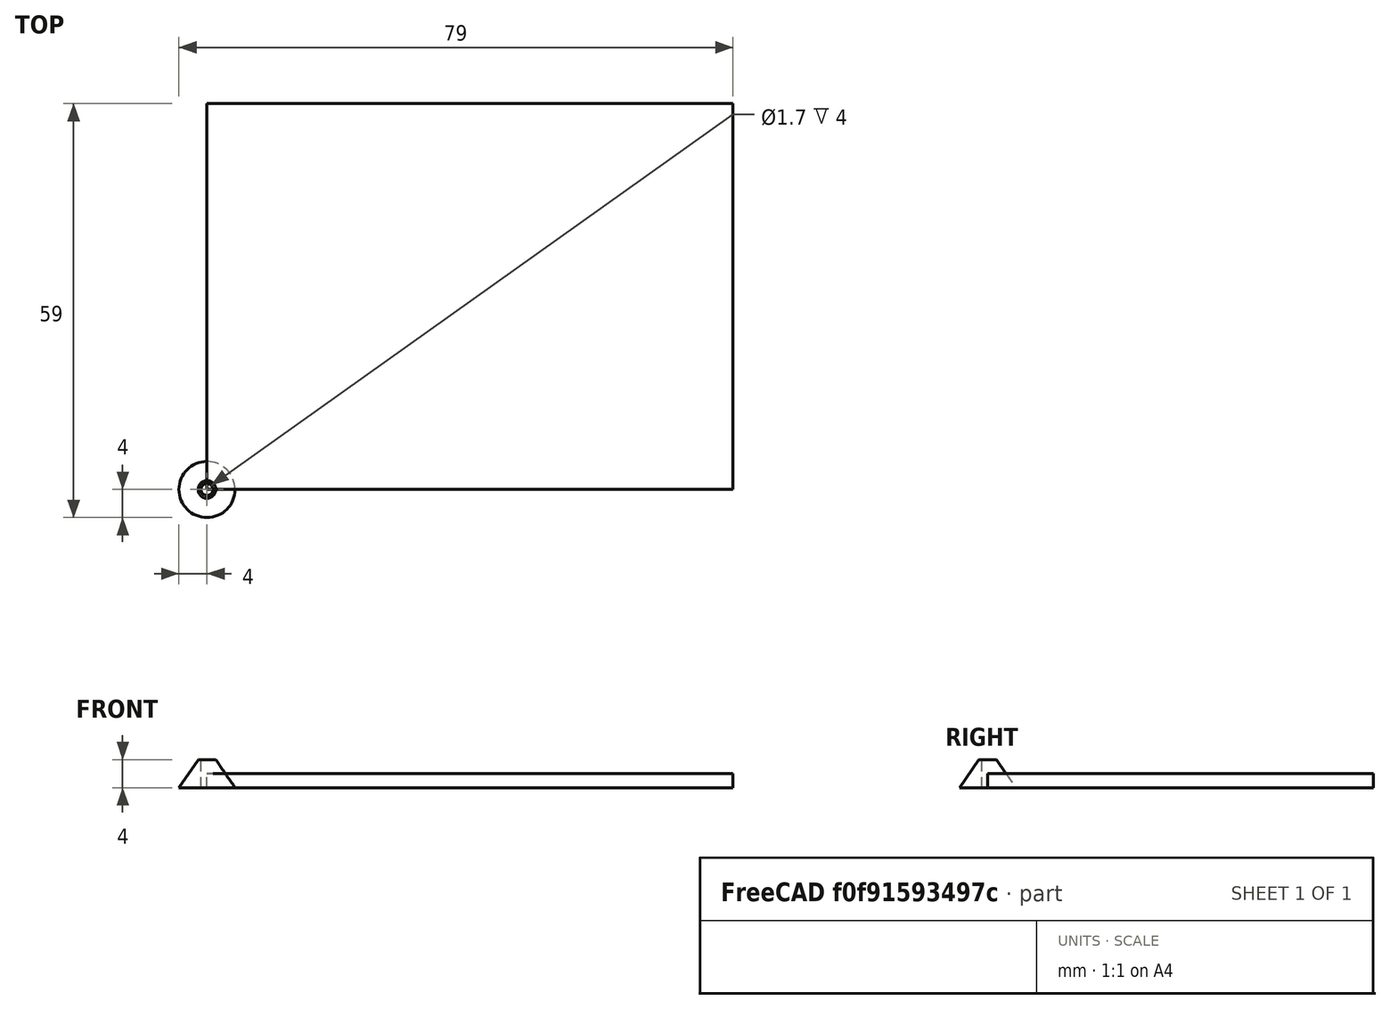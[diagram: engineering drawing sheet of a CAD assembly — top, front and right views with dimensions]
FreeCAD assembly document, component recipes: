
FREECAD ASSEMBLY — COMPONENT RECIPES ("perfboard-standoffs")

This assembly document has 5 components, labeled P0..P4 below (a component is one placed body or linked part). 5 of them carry a construction recipe — the FreeCAD feature program that regenerates the part from scratch, quoted from this document or its linked companion documents; the rest are supplied as boundary geometry only. No exploded tour is included for this assembly.
COMPONENT P0 — recipe-attached ("Body", modeled in this document).
Construction recipe (the document's own serialized feature program — sketch geometry with constraints, then the solid features built on it; lengths are millimeters unless a unit is written):

FEATURE [Sketcher::SketchObject] Sketch003
  ArcFitTolerance = 1e-06
  AttachmentSupport = -> [XY_Plane005]
  FullyConstrained = true
  MakeInternals = false
  MapMode = 5
  sketch-geometry (4):
    g0: LineSegment StartX=0 StartY=0 StartZ=0 EndX=75 EndY=0 EndZ=0
    g1: LineSegment StartX=75 StartY=0 StartZ=0 EndX=75 EndY=55 EndZ=0
    g2: LineSegment StartX=75 StartY=55 StartZ=0 EndX=0 EndY=55 EndZ=0
    g3: LineSegment StartX=0 StartY=55 StartZ=0 EndX=0 EndY=0 EndZ=0
  constraints (11):
    c: Coincident(g0,g1)
    c: Coincident(g1,g2)
    c: Coincident(g2,g3)
    c: Coincident(g3,g0)
    c: Horizontal(g0)
    c: Horizontal(g2)
    c: Vertical(g1)
    c: Vertical(g3)
    c: Distance(g1,g3) = 75
    c: Distance(g0,g2) = 55
    c: Coincident(g0,g-1)
FEATURE [PartDesign::Pad] Pad
  Direction = (0,0,1)
  Length = 2
  Length2 = 10
  Profile = -> Sketch003
  ReferenceAxis = -> Sketch003 [N_Axis]
  Refine = true
  Suppressed = false
  Type = 0
FEATURE [PartDesign::Body] Body001  label="Body"
  AllowCompound = false
  Group = -> [Sketch003,Pad]
  Origin = -> Origin005
  Tip = -> Pad
COMPONENT P1 — recipe-attached ("standoff001", modeled in this document).
Construction recipe (the document's own serialized feature program — sketch geometry with constraints, then the solid features built on it; lengths are millimeters unless a unit is written):

FEATURE [Sketcher::SketchObject] Sketch
  ArcFitTolerance = 1e-06
  AttachmentSupport = -> [XY_Plane001]
  FullyConstrained = true
  MakeInternals = false
  MapMode = 5
  sketch-geometry (1):
    g0: Circle CenterX=0 CenterY=0 CenterZ=0 NormalX=0 NormalY=0 NormalZ=1 AngleXU=0 Radius=4
  constraints (2):
    c: Diameter(g0) = 8
    c: Coincident(g0,g-1)
FEATURE [PartDesign::Plane] DatumPlane
  AttachmentOffset = pos=(0,0,4) rot=(0,0,1;0rad)
  AttachmentSupport = -> [Sketch]
  Length = 60
  MapMode = 2
  Placement = pos=(0,0,4) rot=(0,0,1;0rad)
  ResizeMode = 0
  Width = 60
FEATURE [Sketcher::SketchObject] Sketch001
  ArcFitTolerance = 1e-06
  AttachmentSupport = -> [DatumPlane]
  FullyConstrained = true
  MakeInternals = false
  MapMode = 5
  Placement = pos=(0,0,4) rot=(0,0,1;0rad)
  sketch-geometry (1):
    g0: Circle CenterX=0 CenterY=0 CenterZ=0 NormalX=0 NormalY=0 NormalZ=1 AngleXU=0 Radius=1.25
  constraints (2):
    c: Diameter(g0) = 2.5
    c: Coincident(g0,g-1)
FEATURE [PartDesign::AdditiveLoft] AdditiveLoft
  Closed = false
  Placement = pos=(0,0,4) rot=(0,0,1;0rad)
  Profile = -> Sketch001
  Refine = true
  Ruled = false
  Sections = -> [Sketch]
  Suppressed = false
FEATURE [Sketcher::SketchObject] Sketch002
  ArcFitTolerance = 1e-06
  AttachmentSupport = -> [AdditiveLoft]
  FullyConstrained = true
  MakeInternals = false
  MapMode = 5
  Placement = pos=(0,0,4) rot=(0,0,1;0rad)
  sketch-geometry (1):
    g0: Circle CenterX=0 CenterY=0 CenterZ=0 NormalX=0 NormalY=0 NormalZ=1 AngleXU=0 Radius=0.85
  constraints (2):
    c: Diameter(g0) = 1.7
    c: Coincident(g0,g-1)
FEATURE [PartDesign::Pocket] Pocket
  BaseFeature = -> AdditiveLoft
  Direction = (0,0,-1)
  Length = 5
  Length2 = 5
  Placement = pos=(0,0,4) rot=(0,0,1;0rad)
  Profile = -> Sketch002
  ReferenceAxis = -> Sketch002 [N_Axis]
  Refine = true
  Suppressed = false
  Type = 0
FEATURE [PartDesign::Body] Body  label="standoff"
  AllowCompound = false
  Group = -> [Sketch,DatumPlane,Sketch001,AdditiveLoft,Sketch002,Pocket]
  Origin = -> Origin001
  Tip = -> Pocket
COMPONENT P2 — same part as P1; its construction recipe is shown at P1.
COMPONENT P3 — same part as P1; its construction recipe is shown at P1.
COMPONENT P4 — same part as P1; its construction recipe is shown at P1.
PROVENANCE & LICENSES
A FreeCAD (.FCStd) document from a public repository crawl; recipes are the document's own serialized feature recipes (and, for linked parts, companion documents' recipes).
License: as declared in the source repository (recorded in the dataset sidecar).
